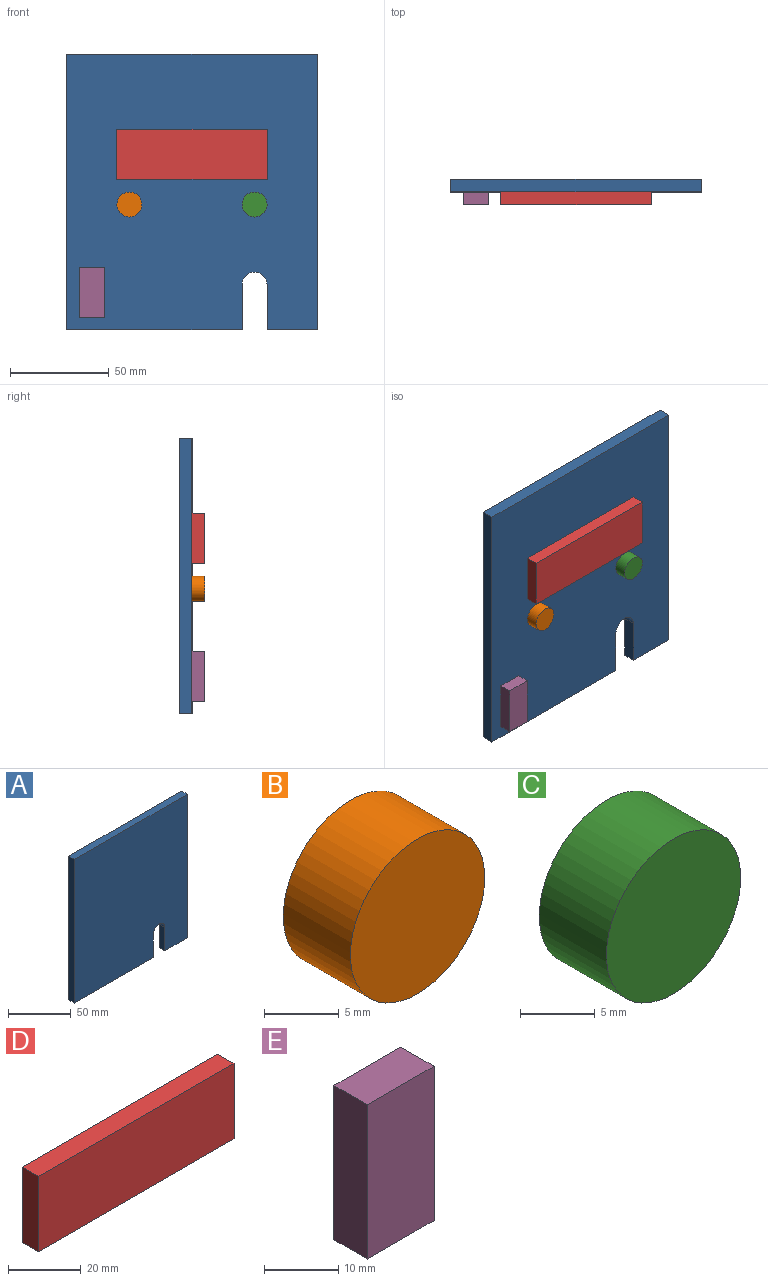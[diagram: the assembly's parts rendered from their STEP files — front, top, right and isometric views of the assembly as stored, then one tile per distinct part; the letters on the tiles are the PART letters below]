
ASSEMBLY  parts=5 mates=4
PART A: 10 faces, bbox 127x6.4x139.7 mm
  f0: plane 88.9x6.35mm, normal (0,0,-1), area 564.5mm2, adj f1,f4,f6,f8
  f1: plane 139.7x127mm, normal (0,1,0), area 17388.2mm2, adj f0,f2,f3,f4,f5,f7,f8,f9
  f2: plane 139.7x6.35mm, normal (1,0,0), area 887.1mm2, adj f1,f3,f5,f6
  f3: plane 127x6.35mm, normal (0,0,1), area 806.5mm2, adj f1,f2,f4,f6
  f4: plane 139.7x6.35mm, normal (-1,0,0), area 887.1mm2, adj f0,f1,f3,f6
  f5: plane 25.4x6.35mm, normal (0,0,-1), area 161.3mm2, adj f1,f2,f6,f9
  f6: plane 139.7x127mm, normal (0,-1,0), area 17388.2mm2, adj f0,f2,f3,f4,f5,f7,f8,f9
  f7: cylinder r=6.35mm len=12.7mm, axis (0,-1,0), area 126.7mm2, adj f1,f6,f8,f9
  f8: plane 22.86x6.35mm, normal (1,0,0), area 145.2mm2, adj f0,f1,f6,f7
  f9: plane 22.86x6.35mm, normal (-1,0,0), area 145.2mm2, adj f1,f5,f6,f7
PART B: 3 faces, bbox 12.7x6.4x12.7 mm
  f0: cylinder r=6.35mm len=12.7mm, axis (0,1,0), area 253.4mm2, adj f1,f2
  f1: plane 12.7x12.7mm, normal (0,-1,0), area 126.7mm2, adj f0
  f2: plane 12.7x12.7mm, normal (0,1,0), area 126.7mm2, adj f0
PART C: 3 faces, bbox 12.7x6.4x12.7 mm
  f0: cylinder r=6.35mm len=12.7mm, axis (0,1,0), area 253.4mm2, adj f1,f2
  f1: plane 12.7x12.7mm, normal (0,-1,0), area 126.7mm2, adj f0
  f2: plane 12.7x12.7mm, normal (0,1,0), area 126.7mm2, adj f0
PART D: 6 faces, bbox 76.2x6.4x25.4 mm
  f0: plane 25.4x6.35mm, normal (1,0,0), area 161.3mm2, adj f1,f3,f4,f5
  f1: plane 76.2x6.35mm, normal (0,0,1), area 483.9mm2, adj f0,f2,f4,f5
  f2: plane 25.4x6.35mm, normal (-1,0,0), area 161.3mm2, adj f1,f3,f4,f5
  f3: plane 76.2x6.35mm, normal (0,0,-1), area 483.9mm2, adj f0,f2,f4,f5
  f4: plane 76.2x25.4mm, normal (0,1,0), area 1935.5mm2, adj f0,f1,f2,f3
  f5: plane 76.2x25.4mm, normal (0,-1,0), area 1935.5mm2, adj f0,f1,f2,f3
PART E: 6 faces, bbox 12.7x6.4x25.4 mm
  f0: plane 25.4x6.35mm, normal (1,0,0), area 161.3mm2, adj f1,f3,f4,f5
  f1: plane 12.7x6.35mm, normal (0,0,1), area 80.6mm2, adj f0,f2,f4,f5
  f2: plane 25.4x6.35mm, normal (-1,0,0), area 161.3mm2, adj f1,f3,f4,f5
  f3: plane 12.7x6.35mm, normal (0,0,-1), area 80.6mm2, adj f0,f2,f4,f5
  f4: plane 25.4x12.7mm, normal (0,-1,0), area 322.6mm2, adj f0,f1,f2,f3
  f5: plane 25.4x12.7mm, normal (0,1,0), area 322.6mm2, adj f0,f1,f2,f3
PLACE A t=(81.77,99.74,-2.78)mm
PLACE B t=(81.77,99.74,-2.78)mm
PLACE C t=(81.77,99.74,-2.78)mm
PLACE D t=(81.77,93.39,-2.78)mm
PLACE E t=(81.77,99.74,-2.78)mm
MATE fastened D.f4 <-> A.f6  axis (0,1,0) through (32.88,93.39,92)mm
MATE fastened E.f5 <-> A.f6  axis (0,1,0) through (32.88,93.39,-47.7)mm
MATE fastened B.f2 <-> A.f6  axis (0,1,0) through (32.88,93.39,92)mm
MATE fastened C.f2 <-> A.f6  axis (0,1,0) through (159.88,93.39,92)mm
